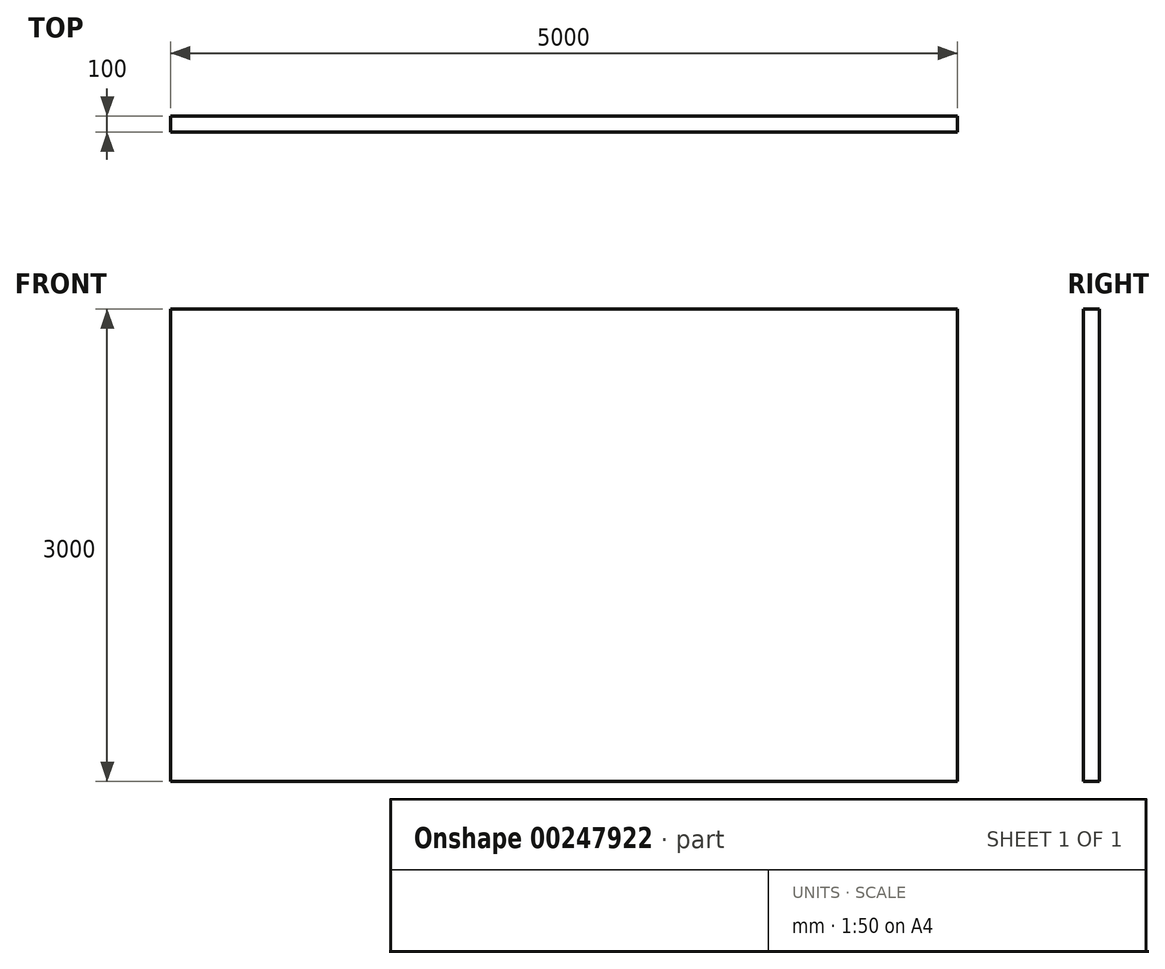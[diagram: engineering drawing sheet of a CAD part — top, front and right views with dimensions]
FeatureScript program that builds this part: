
annotation { "Feature Type Name" : "Feature", "Feature Type Description" : "" }
export const myFeature = defineFeature(function(context is Context, id is Id, definition is map)
    precondition{}
    {
        {
            var Q0;
            Q0=qCreatedBy(makeId("Front.planeOp"),FACE);
            var sketch = newSketch(context, id + "F0", { "sketchPlane" : qUnion([Q0])});
            skLineSegment(sketch, "E0.bottom", {"start": v(2500, 0) * mm, "end": v(-2500, 0) * mm});
            skLineSegment(sketch, "E0.top", {"start": v(2500, 3000) * mm, "end": v(-2500, 3000) * mm});
            skLineSegment(sketch, "E0.left", {"start": v(2500, 0) * mm, "end": v(2500, 3000) * mm});
            skLineSegment(sketch, "E0.right", {"start": v(-2500, 0) * mm, "end": v(-2500, 3000) * mm});
            skPoint(sketch, "E0.middle", {"position": v(0, 1500) * mm});
            skSolve(sketch);
        }
        {
            var Q0;
            Q0=makeQuery(id+"F0.imprint","IMPRINT",FACE,{"disambiguationData":[TD([[makeQuery(id+"F0.imprint","IMPRINT",EDGE,{"derivedFrom":sQuery(id+"F0.wireOp",EDGE,"E0.bottom")}),-1.0]])]});
            extrude(context, id + "F1", {"entities" : qUnion([Q0]), "endBound" : BoundingType.SYMMETRIC, "depth" : 100 * mm});
        }
    });
